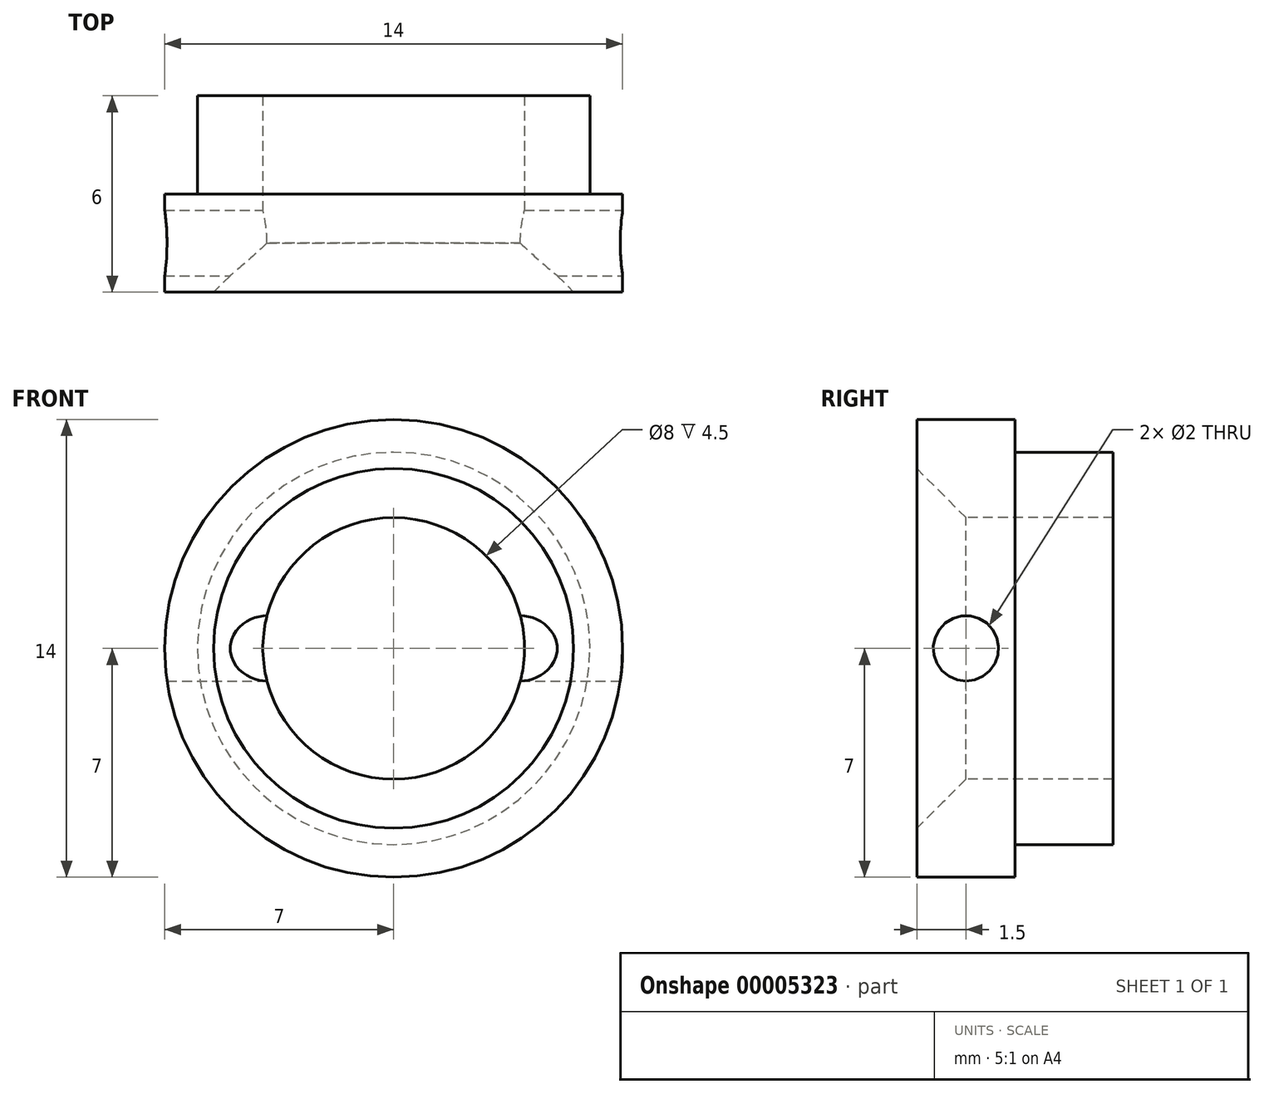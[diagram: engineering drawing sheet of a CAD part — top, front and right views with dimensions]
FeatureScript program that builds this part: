
annotation { "Feature Type Name" : "Feature", "Feature Type Description" : "" }
export const myFeature = defineFeature(function(context is Context, id is Id, definition is map)
    precondition{}
    {
        {
            var Q0;
            Q0=qCreatedBy(makeId("Front.planeOp"),FACE);
            var sketch = newSketch(context, id + "F0", { "sketchPlane" : qUnion([Q0])});
            skCircle(sketch, "E0", {"center": v(0, 0) * mm, "radius": 4 * mm});
            skCircle(sketch, "E1", {"center": v(0, 0) * mm, "radius": 6 * mm});
            skCircle(sketch, "E2", {"center": v(0, 0) * mm, "radius": 7 * mm});
            skSolve(sketch);
        }
        {
            var Q0;
            Q0=makeQuery(id+"F0.imprint","IMPRINT",FACE,{"disambiguationData":[TD([[makeQuery(id+"F0.imprint","IMPRINT",EDGE,{"derivedFrom":sQuery(id+"F0.wireOp",EDGE,"E0")}),-1.0]])]});
            extrude(context, id + "F1", {"entities" : qUnion([Q0]), "oppositeDirection" : true, "depth" : 3 * mm});
        }
        {
            var Q0;
            Q0=makeQuery(id+"F0.imprint","IMPRINT",FACE,{"disambiguationData":[TD([[makeQuery(id+"F0.imprint","IMPRINT",EDGE,{"derivedFrom":sQuery(id+"F0.wireOp",EDGE,"E0")}),-1.0]])]});
            var Q1;
            Q1=makeQuery(id+"F0.imprint","IMPRINT",FACE,{"disambiguationData":[TD([[makeQuery(id+"F0.imprint","IMPRINT",EDGE,{"derivedFrom":sQuery(id+"F0.wireOp",EDGE,"E1")}),-1.0]])]});
            extrude(context, id + "F2", {"entities" : qUnion([Q0, Q1]), "operationType" : NewBodyOperationType.ADD, "depth" : 3 * mm});
        }
        {
            var Q0;
            Q0=makeQuery(id+"F2.opExtrude","CAP_EDGE",EDGE,{"disambiguationData":[OSD([sQuery(id+"F0.wireOp",EDGE,"E0")])],"isStart":false});
            chamfer(context, id + "F3", {"entities" : qUnion([Q0]), "width" : 1.5 * mm, "tangentPropagation" : true});
        }
        {
            var Q0;
            Q0=qCreatedBy(makeId("Right.planeOp"),FACE);
            var sketch = newSketch(context, id + "F4", { "sketchPlane" : qUnion([Q0])});
            skCircle(sketch, "E3", {"center": v(-1.5, 0) * mm, "radius": 1 * mm});
            skSolve(sketch);
        }
        {
            var Q0;
            Q0=makeQuery(id+"F4.imprint","IMPRINT",FACE,{"disambiguationData":[TD([[makeQuery(id+"F4.imprint","IMPRINT",EDGE,{"derivedFrom":sQuery(id+"F4.wireOp",EDGE,"E3")}),1.0]])]});
            extrude(context, id + "F5", {"entities" : qUnion([Q0]), "operationType" : NewBodyOperationType.REMOVE, "endBound" : BoundingType.SYMMETRIC, "oppositeDirection" : true, "depth" : 25 * mm});
        }
    });
